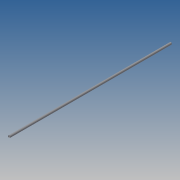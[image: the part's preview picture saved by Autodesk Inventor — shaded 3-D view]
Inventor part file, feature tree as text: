
AUTODESK INVENTOR PART (.ipt)
format: ipt  version: 2014 SP1 (Build 180222100, 222)  size: 67,072 bytes
history: native  units: in
note: dims shown in document units (in); Inventor stores cm internally (conversion verified against a paired STEP export)
features: extrude x1, sketch x1
ambient origin geometry x8: Origin, YZ Plane, XZ Plane, XY Plane, X Axis, Y Axis, Z Axis, Center Point
bodies: Solid1 (feature_tree)
feature tree (2):
  extrude  "Extrusion1"  Depth=452.7559in
  sketch  "Sketch1"  dims[d1=0.2in d2=6.0in d3=452.7559in d4=0.0in]
